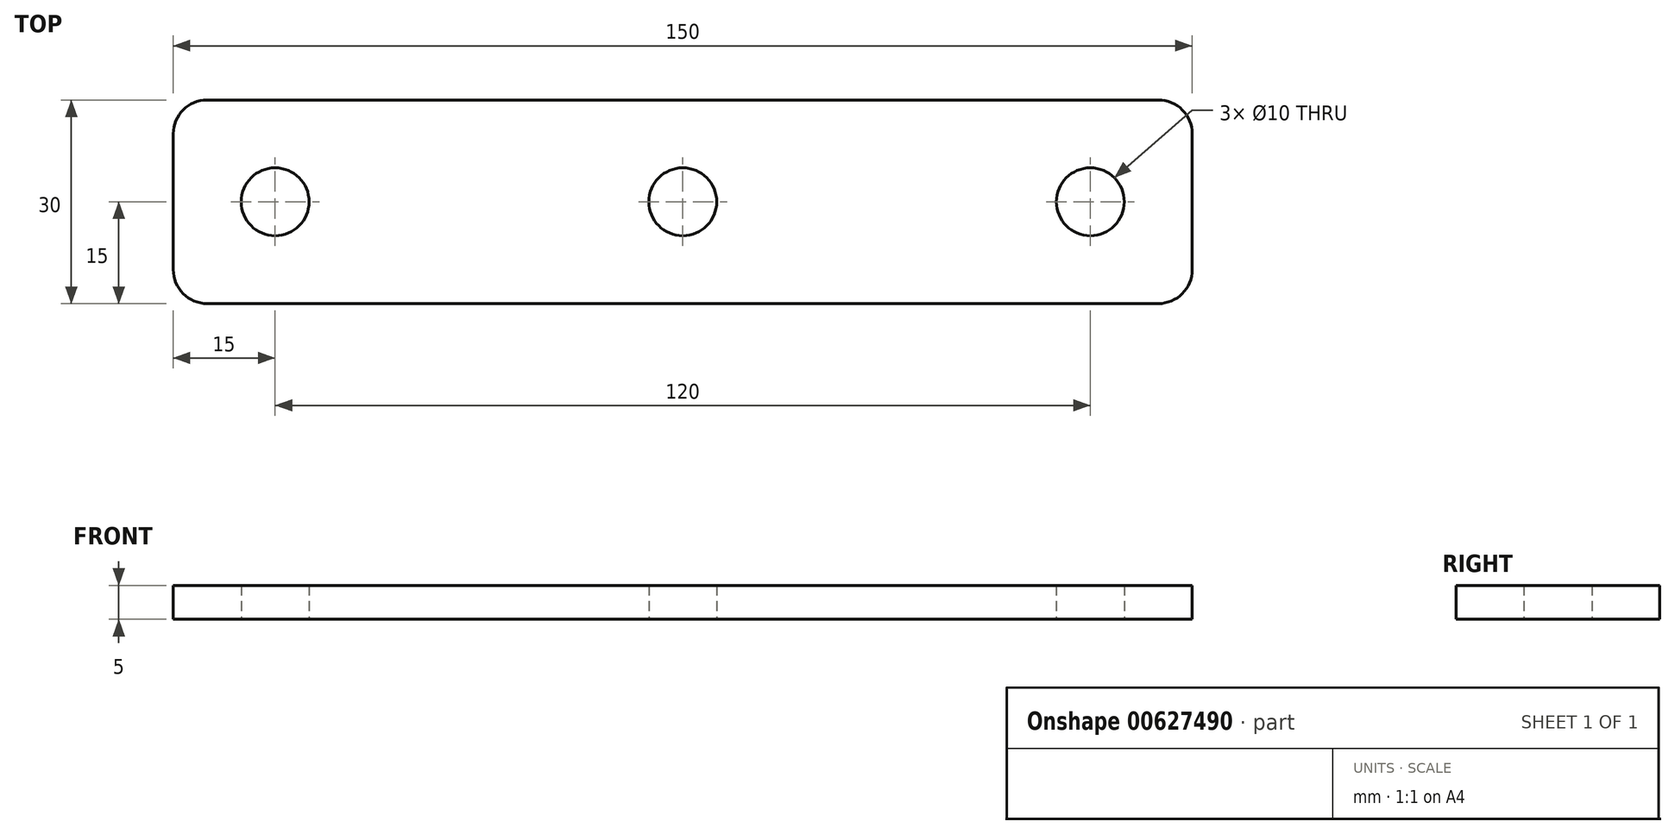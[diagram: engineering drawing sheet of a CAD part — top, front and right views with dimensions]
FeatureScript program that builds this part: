
annotation { "Feature Type Name" : "Feature", "Feature Type Description" : "" }
export const myFeature = defineFeature(function(context is Context, id is Id, definition is map)
    precondition{}
    {
        {
            var Q0;
            Q0=qCreatedBy(makeId("Top.planeOp"),FACE);
            var sketch = newSketch(context, id + "F0", { "sketchPlane" : qUnion([Q0])});
            skLineSegment(sketch, "E0.bottom", {"start": v(-70, 15) * mm, "end": v(70, 15) * mm});
            skLineSegment(sketch, "E0.top", {"start": v(-70, -15) * mm, "end": v(70, -15) * mm});
            skLineSegment(sketch, "E0.left", {"start": v(-75, 10) * mm, "end": v(-75, -10) * mm});
            skLineSegment(sketch, "E0.right", {"start": v(75, 10) * mm, "end": v(75, -10) * mm});
            skPoint(sketch, "E0.middle", {"position": v(0, 0) * mm});
            skArc(sketch, "E1", {"start": v(-60, 5) * mm, "mid": v(-65, 0) * mm, "end": v(-60, -5) * mm});
            skArc(sketch, "E2.MirrorC", {"start": v(60, 5) * mm, "mid": v(65, 0) * mm, "end": v(60, -5) * mm});
            skPoint(sketch, "E3.visualSharp", {"position": v(-75, 15) * mm});
            skArc(sketch, "E3.filletArc", {"start": v(-70, 15) * mm, "mid": v(-73.54, 13.54) * mm, "end": v(-75, 10) * mm});
            skPoint(sketch, "E4.visualSharp", {"position": v(-75, -15) * mm});
            skArc(sketch, "E4.filletArc", {"start": v(-75, -10) * mm, "mid": v(-73.54, -13.54) * mm, "end": v(-70, -15) * mm});
            skPoint(sketch, "E5.visualSharp", {"position": v(75, 15) * mm});
            skArc(sketch, "E5.filletArc", {"start": v(75, 10) * mm, "mid": v(73.54, 13.54) * mm, "end": v(70, 15) * mm});
            skPoint(sketch, "E6.visualSharp", {"position": v(75, -15) * mm});
            skArc(sketch, "E6.filletArc", {"start": v(70, -15) * mm, "mid": v(73.54, -13.54) * mm, "end": v(75, -10) * mm});
            skArc(sketch, "E7", {"start": v(-60, -5) * mm, "mid": v(-55, 0) * mm, "end": v(-60, 5) * mm});
            skArc(sketch, "E8", {"start": v(60, 5) * mm, "mid": v(55, 0) * mm, "end": v(60, -5) * mm});
            skArc(sketch, "E9", {"start": v(0, 5) * mm, "mid": v(-5, 0) * mm, "end": v(0, -5) * mm});
            skArc(sketch, "E10", {"start": v(0, -5) * mm, "mid": v(5, 0) * mm, "end": v(0, 5) * mm});
            skSolve(sketch);
        }
        {
            var Q0;
            Q0=qSketchRegion(id+"F0",true);
            extrude(context, id + "F1", {"entities" : qUnion([Q0]), "depth" : 5 * mm, "offsetDistance" : 25 * mm});
        }
    });
